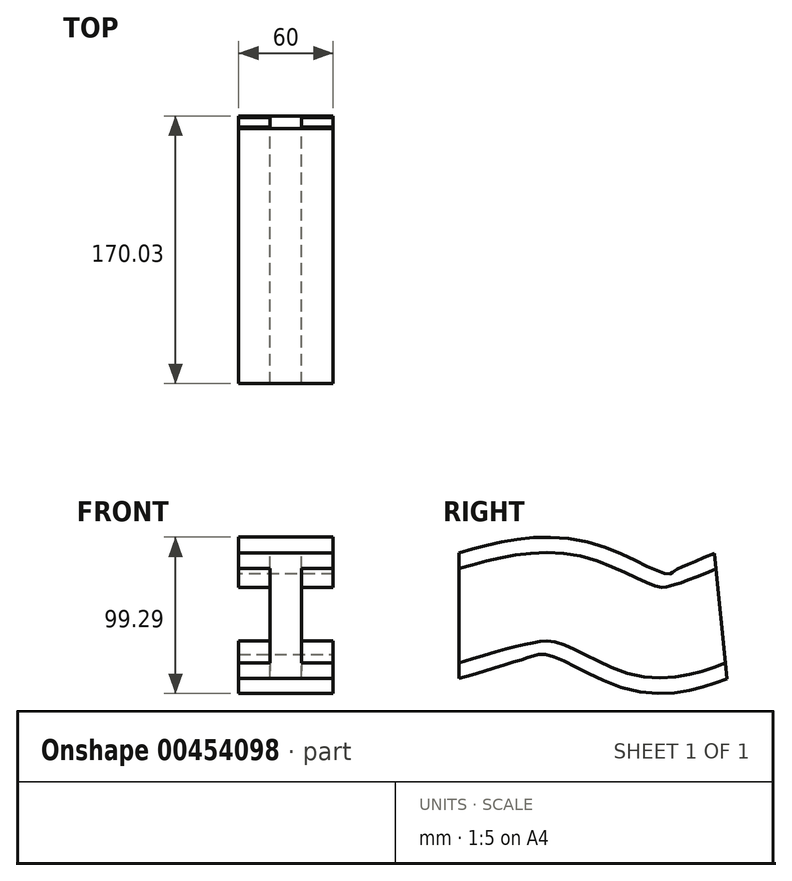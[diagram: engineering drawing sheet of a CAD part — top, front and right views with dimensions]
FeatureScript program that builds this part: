
annotation { "Feature Type Name" : "Feature", "Feature Type Description" : "" }
export const myFeature = defineFeature(function(context is Context, id is Id, definition is map)
    precondition{}
    {
        {
            var Q0;
            Q0=qCreatedBy(makeId("Front.planeOp"),FACE);
            var sketch = newSketch(context, id + "F0", { "sketchPlane" : qUnion([Q0])});
            skLineSegment(sketch, "E0", {"start": v(-30, 40) * mm, "end": v(30, 40) * mm});
            skLineSegment(sketch, "E1", {"start": v(30, 40) * mm, "end": v(30, 30) * mm});
            skLineSegment(sketch, "E2", {"start": v(30, 30) * mm, "end": v(10, 30) * mm});
            skLineSegment(sketch, "E3", {"start": v(10, 30) * mm, "end": v(10, -30) * mm});
            skLineSegment(sketch, "E4", {"start": v(10, -30) * mm, "end": v(30, -30) * mm});
            skLineSegment(sketch, "E5", {"start": v(30, -30) * mm, "end": v(30, -40) * mm});
            skLineSegment(sketch, "E6", {"start": v(30, -40) * mm, "end": v(-30, -40) * mm});
            skLineSegment(sketch, "E7", {"start": v(-30, -40) * mm, "end": v(-30, -30) * mm});
            skLineSegment(sketch, "E8", {"start": v(-30, -30) * mm, "end": v(-10, -30) * mm});
            skLineSegment(sketch, "E9", {"start": v(-10, -30) * mm, "end": v(-10, 30) * mm});
            skLineSegment(sketch, "E10", {"start": v(-10, 30) * mm, "end": v(-30, 30) * mm});
            skLineSegment(sketch, "E11", {"start": v(-30, 30) * mm, "end": v(-30, 40) * mm});
            skSolve(sketch);
        }
        {
            var Q0;
            Q0=qCreatedBy(makeId("Right.planeOp"),FACE);
            var sketch = newSketch(context, id + "F1", { "sketchPlane" : qUnion([Q0])});
            skFitSpline(sketch, "E12", {"points": [v(2.92, 0) * mm, v(69.42, 9.01) * mm, v(121.27, -10.25) * mm, v(168.94, 0) * mm], "startDerivative": vector(190.56, 54.77) * mm, "endDerivative": vector(155.14, 61.97) * mm});
            skSolve(sketch);
        }
        {
            var Q0;
            Q0 = qSketchRegion(id + "F0", true);
            var Q1;
            Q1 = qConstructionFilter(qBodyType(qCreatedBy(id + "F1" ,EDGE), BodyType.WIRE), ConstructionObject.NO);
            sweep(context, id + "F2", {"profiles" : qUnion([Q0]), "path" : qUnion([Q1])});
        }
    });
